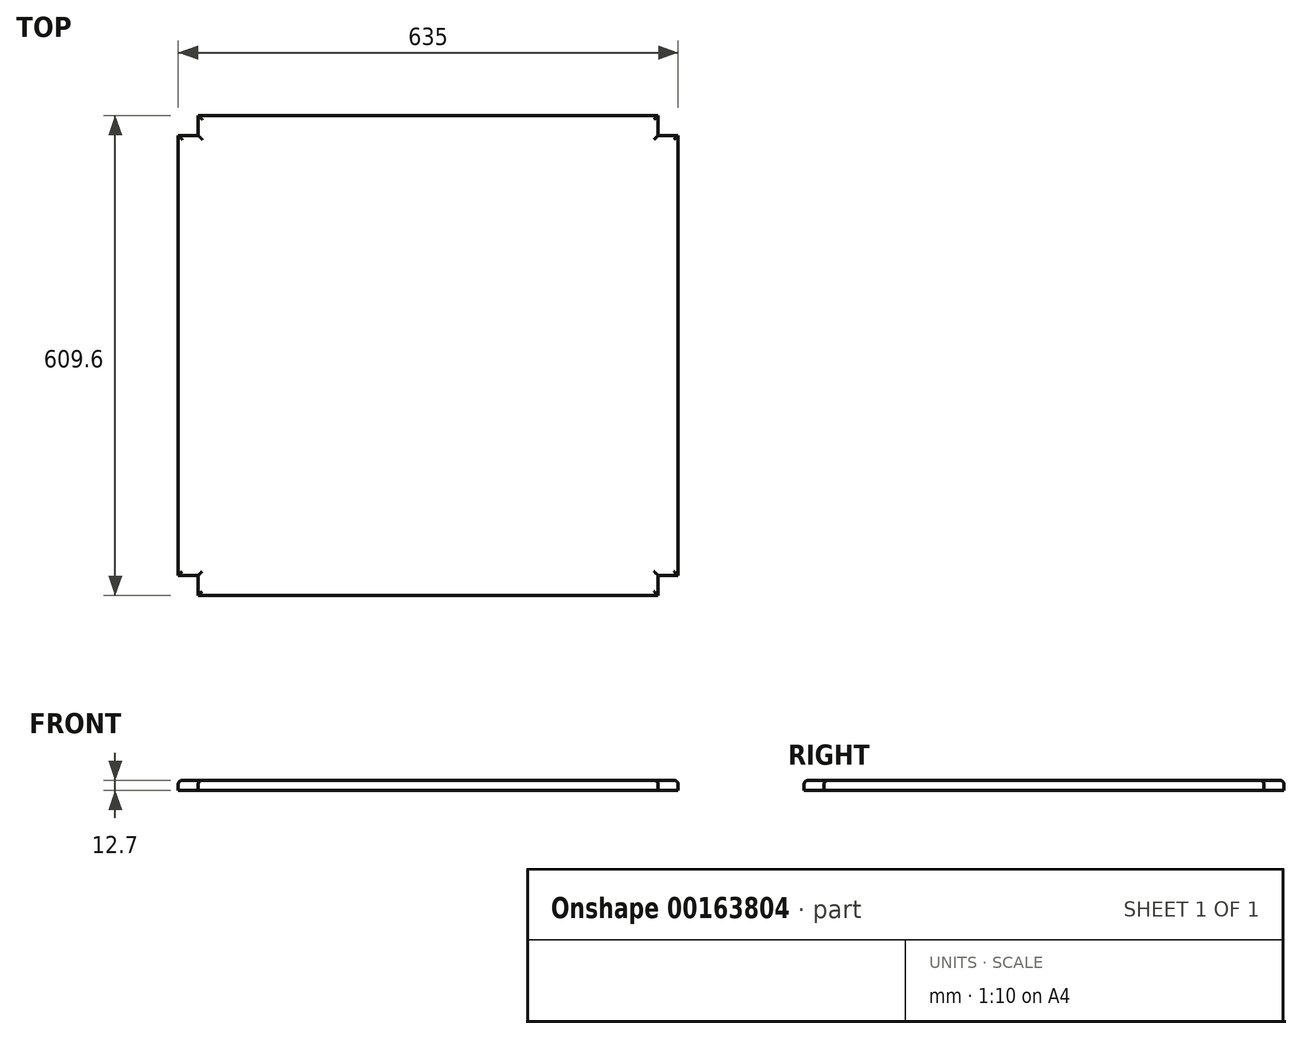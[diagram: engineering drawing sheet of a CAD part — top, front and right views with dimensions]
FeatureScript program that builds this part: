
annotation { "Feature Type Name" : "Feature", "Feature Type Description" : "" }
export const myFeature = defineFeature(function(context is Context, id is Id, definition is map)
    precondition{}
    {
        {
            var Q0;
            Q0=qCreatedBy(makeId("Top.planeOp"),FACE);
            var sketch = newSketch(context, id + "F0", { "sketchPlane" : qUnion([Q0])});
            skLineSegment(sketch, "E0.bottom", {"start": v(284.02, -284.44) * mm, "end": v(-300.18, -284.44) * mm});
            skLineSegment(sketch, "E0.top", {"start": v(284.02, 325.16) * mm, "end": v(-300.18, 325.16) * mm});
            skPoint(sketch, "E0.middle", {"position": v(0, 0) * mm});
            skLineSegment(sketch, "E1.trimOffspring", {"start": v(-325.58, -259.04) * mm, "end": v(-325.58, 299.76) * mm});
            skLineSegment(sketch, "E2", {"start": v(0, 0) * mm, "end": v(0, 342.9) * mm, "construction": true});
            skLineSegment(sketch, "E3", {"start": v(309.42, -259.04) * mm, "end": v(309.42, 299.76) * mm});
            skLineSegment(sketch, "E4", {"start": v(0, 0) * mm, "end": v(558.8, 0) * mm, "construction": true});
            skLineSegment(sketch, "E5.top", {"start": v(309.42, 299.76) * mm, "end": v(284.02, 299.76) * mm});
            skLineSegment(sketch, "E5.right", {"start": v(284.02, 325.16) * mm, "end": v(284.02, 299.76) * mm});
            skLineSegment(sketch, "E6.top", {"start": v(309.42, -259.04) * mm, "end": v(284.02, -259.04) * mm});
            skLineSegment(sketch, "E6.right", {"start": v(284.02, -284.44) * mm, "end": v(284.02, -259.04) * mm});
            skLineSegment(sketch, "E7.top", {"start": v(-325.58, -259.04) * mm, "end": v(-300.18, -259.04) * mm});
            skLineSegment(sketch, "E7.right", {"start": v(-300.18, -284.44) * mm, "end": v(-300.18, -259.04) * mm});
            skLineSegment(sketch, "E8.top", {"start": v(-325.58, 299.76) * mm, "end": v(-300.18, 299.76) * mm});
            skLineSegment(sketch, "E8.right", {"start": v(-300.18, 325.16) * mm, "end": v(-300.18, 299.76) * mm});
            skSolve(sketch);
        }
        {
            var Q0;
            Q0=qSketchRegion(id+"F0",true);
            extrude(context, id + "F1", {"entities" : qUnion([Q0]), "depth" : 12.7 * mm});
        }
        {
            var Q0;
            Q0=makeQuery(id+"F1.opExtrude","CAP_FACE",FACE,{"disambiguationData":[OSD([sQuery(id+"F0.wireOp",EDGE,"E0.bottom"),sQuery(id+"F0.wireOp",EDGE,"E0.top"),sQuery(id+"F0.wireOp",EDGE,"E0.left"),sQuery(id+"F0.wireOp",EDGE,"E0.right"),sQuery(id+"F0.wireOp",EDGE,"b15ae54a-3f8c-4f60-8baa-cd31eb437c6e.filletArc"),sQuery(id+"F0.wireOp",EDGE,"aa749b1a-4f62-40e5-a9dd-a47ec50e650c.filletArc"),sQuery(id+"F0.wireOp",EDGE,"2b33ca63-df12-433b-986b-ef48bfc9de00.filletArc"),sQuery(id+"F0.wireOp",EDGE,"b19e8cbf-3efd-47e7-9b03-fc77b71e0aba.filletArc")])],"isStart":false});
            fillet(context, id + "F2", {"entities" : qUnion([Q0]), "radius" : 5.08 * mm, "tangentPropagation" : true, "allowEdgeOverflow" : false});
        }
    });
